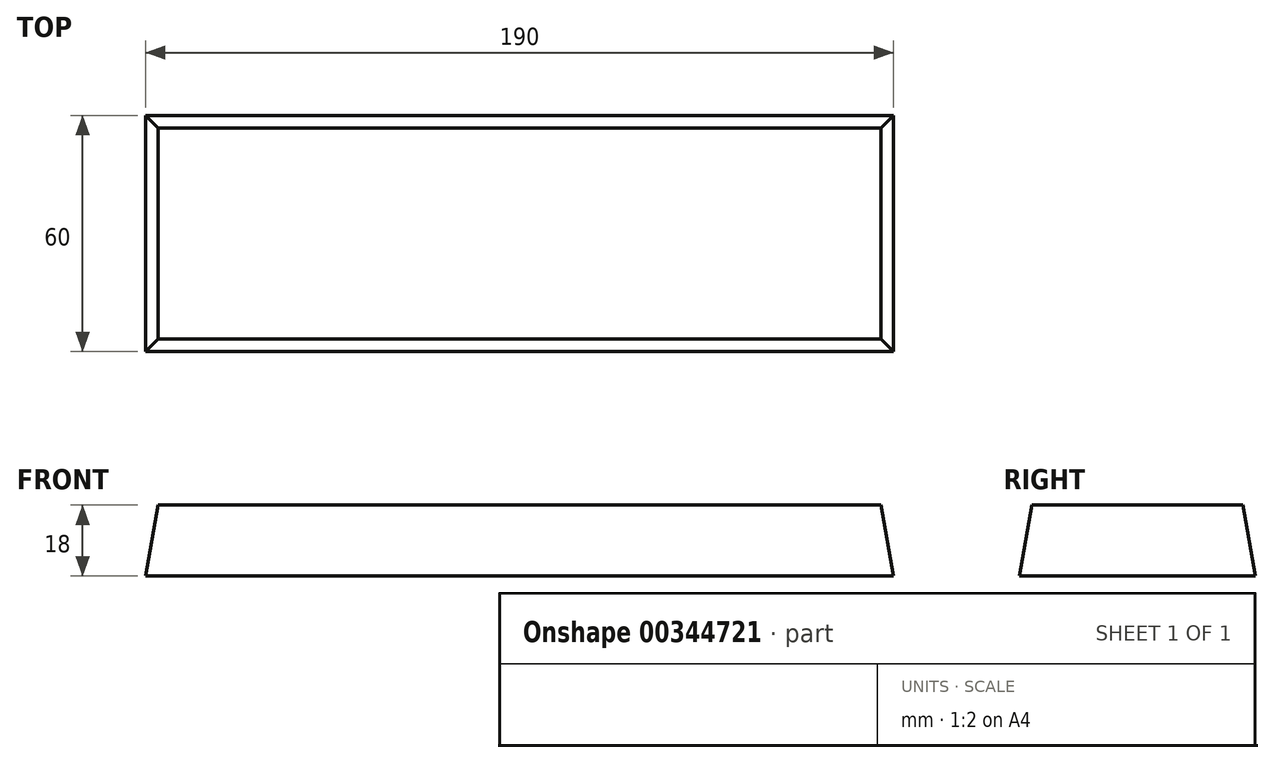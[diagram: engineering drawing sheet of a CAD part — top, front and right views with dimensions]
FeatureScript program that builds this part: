
annotation { "Feature Type Name" : "Feature", "Feature Type Description" : "" }
export const myFeature = defineFeature(function(context is Context, id is Id, definition is map)
    precondition{}
    {
        {
            var Q0;
            Q0=qCreatedBy(makeId("Top.planeOp"),FACE);
            var sketch = newSketch(context, id + "F0", { "sketchPlane" : qUnion([Q0])});
            skLineSegment(sketch, "E0.bottom", {"start": v(0, 0) * mm, "end": v(190, 0) * mm});
            skLineSegment(sketch, "E0.top", {"start": v(0, 60) * mm, "end": v(190, 60) * mm});
            skLineSegment(sketch, "E0.left", {"start": v(0, 0) * mm, "end": v(0, 60) * mm});
            skLineSegment(sketch, "E0.right", {"start": v(190, 0) * mm, "end": v(190, 60) * mm});
            skSolve(sketch);
        }
        {
            var Q0;
            Q0 = qSketchRegion(id + "F0", true);
            extrude(context, id + "F1", {"entities" : qUnion([Q0]), "depth" : 18 * mm, "hasDraft" : true, "draftAngle" : 10 * degree, "draftPullDirection" : true});
        }
    });
